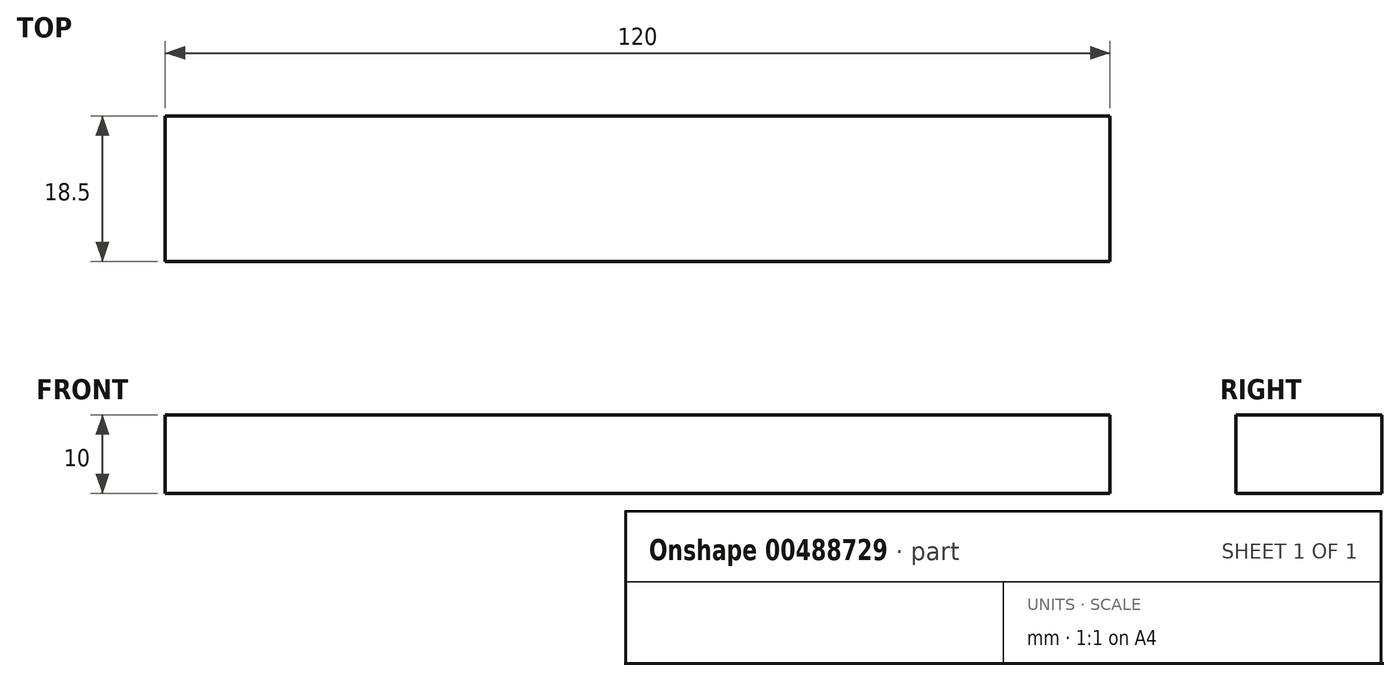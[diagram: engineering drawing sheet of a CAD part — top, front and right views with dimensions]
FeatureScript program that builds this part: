
annotation { "Feature Type Name" : "Feature", "Feature Type Description" : "" }
export const myFeature = defineFeature(function(context is Context, id is Id, definition is map)
    precondition{}
    {
        {
            var Q0;
            Q0=qCreatedBy(makeId("Top.planeOp"),FACE);
            var sketch = newSketch(context, id + "F0", { "sketchPlane" : qUnion([Q0])});
            skLineSegment(sketch, "E0.bottom", {"start": v(60, -9.25) * mm, "end": v(-60, -9.25) * mm});
            skLineSegment(sketch, "E0.top", {"start": v(60, 9.25) * mm, "end": v(-60, 9.25) * mm});
            skLineSegment(sketch, "E0.left", {"start": v(60, -9.25) * mm, "end": v(60, 9.25) * mm});
            skLineSegment(sketch, "E0.right", {"start": v(-60, -9.25) * mm, "end": v(-60, 9.25) * mm});
            skPoint(sketch, "E0.middle", {"position": v(0, 0) * mm});
            skSolve(sketch);
        }
        {
            var Q0;
            Q0 = qSketchRegion(id + "F0", true);
            extrude(context, id + "F1", {"entities" : qUnion([Q0]), "endBound" : BoundingType.SYMMETRIC, "depth" : 10 * mm});
        }
    });
